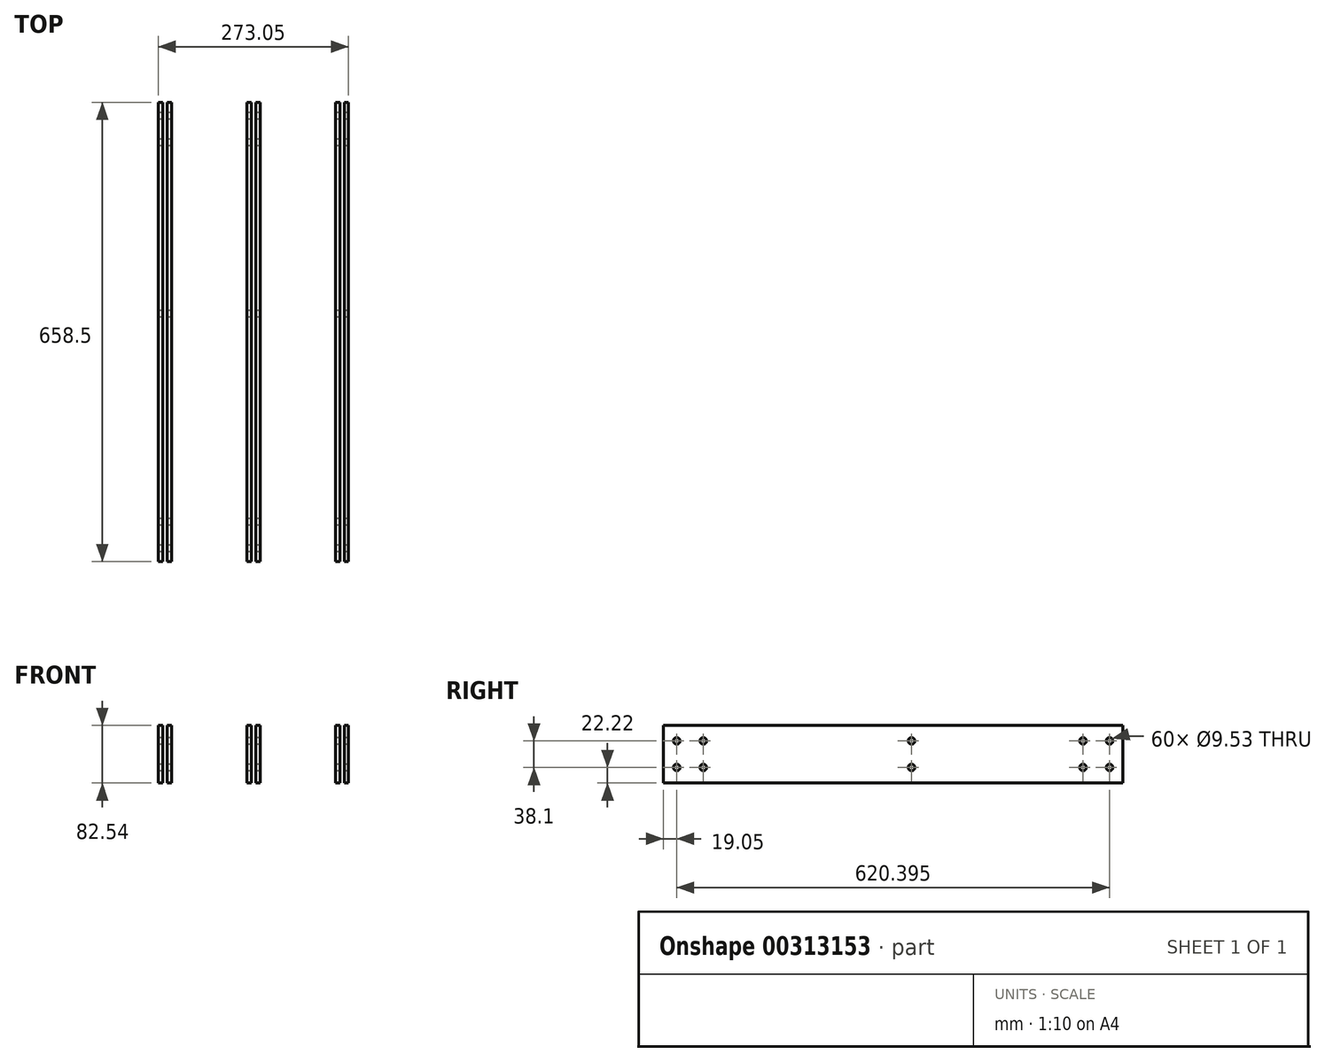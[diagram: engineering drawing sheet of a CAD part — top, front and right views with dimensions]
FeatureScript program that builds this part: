
annotation { "Feature Type Name" : "Feature", "Feature Type Description" : "" }
export const myFeature = defineFeature(function(context is Context, id is Id, definition is map)
    precondition{}
    {
        {
            var Q0;
            Q0=qCreatedBy(makeId("Top.planeOp"),FACE);
            var sketch = newSketch(context, id + "F0", { "sketchPlane" : qUnion([Q0])});
            skLineSegment(sketch, "E0.bottom", {"start": v(0, 0) * mm, "end": v(6.35, 0) * mm});
            skLineSegment(sketch, "E0.top", {"start": v(0, 658.5) * mm, "end": v(6.35, 658.5) * mm});
            skLineSegment(sketch, "E0.left", {"start": v(0, 0) * mm, "end": v(0, 658.5) * mm});
            skLineSegment(sketch, "E0.right", {"start": v(6.35, 0) * mm, "end": v(6.35, 658.5) * mm});
            skLineSegment(sketch, "E1.1.0.0", {"start": v(133.35, 0) * mm, "end": v(133.35, 658.5) * mm});
            skLineSegment(sketch, "E1.1.0.1", {"start": v(127, 0) * mm, "end": v(127, 658.5) * mm});
            skLineSegment(sketch, "E1.1.0.2", {"start": v(127, 658.5) * mm, "end": v(133.35, 658.5) * mm});
            skLineSegment(sketch, "E1.1.0.3", {"start": v(127, 0) * mm, "end": v(133.35, 0) * mm});
            skLineSegment(sketch, "E1.2.0.0", {"start": v(260.35, 0) * mm, "end": v(260.35, 658.5) * mm});
            skLineSegment(sketch, "E1.2.0.1", {"start": v(254, 0) * mm, "end": v(254, 658.5) * mm});
            skLineSegment(sketch, "E1.2.0.2", {"start": v(254, 658.5) * mm, "end": v(260.35, 658.5) * mm});
            skLineSegment(sketch, "E1.2.0.3", {"start": v(254, 0) * mm, "end": v(260.35, 0) * mm});
            skLineSegment(sketch, "E1.direction1", {"start": v(0, 0) * mm, "end": v(127, 0) * mm, "construction": true});
            skSolve(sketch);
        }
        {
            var Q0;
            Q0=qCreatedBy(makeId("Top.planeOp"),FACE);
            var sketch = newSketch(context, id + "F1", { "sketchPlane" : qUnion([Q0])});
            skLineSegment(sketch, "E2.bottom", {"start": v(12.7, 0) * mm, "end": v(19.05, 0) * mm});
            skLineSegment(sketch, "E2.top", {"start": v(12.7, 658.5) * mm, "end": v(19.05, 658.5) * mm});
            skLineSegment(sketch, "E2.left", {"start": v(12.7, 0) * mm, "end": v(12.7, 658.5) * mm});
            skLineSegment(sketch, "E2.right", {"start": v(19.05, 0) * mm, "end": v(19.05, 658.5) * mm});
            skLineSegment(sketch, "E3.1.0.0", {"start": v(146.05, 0) * mm, "end": v(146.05, 658.5) * mm});
            skLineSegment(sketch, "E3.1.0.1", {"start": v(139.7, 0) * mm, "end": v(139.7, 658.5) * mm});
            skLineSegment(sketch, "E3.1.0.2", {"start": v(139.7, 658.5) * mm, "end": v(146.05, 658.5) * mm});
            skLineSegment(sketch, "E3.1.0.3", {"start": v(139.7, 0) * mm, "end": v(146.05, 0) * mm});
            skLineSegment(sketch, "E3.2.0.0", {"start": v(273.05, 0) * mm, "end": v(273.05, 658.5) * mm});
            skLineSegment(sketch, "E3.2.0.1", {"start": v(266.7, 0) * mm, "end": v(266.7, 658.5) * mm});
            skLineSegment(sketch, "E3.2.0.2", {"start": v(266.7, 658.5) * mm, "end": v(273.05, 658.5) * mm});
            skLineSegment(sketch, "E3.2.0.3", {"start": v(266.7, 0) * mm, "end": v(273.05, 0) * mm});
            skLineSegment(sketch, "E3.direction1", {"start": v(12.7, 0) * mm, "end": v(139.7, 0) * mm, "construction": true});
            skSolve(sketch);
        }
        {
            var Q0;
            Q0=qSketchRegion(id+"F0",true);
            var Q1;
            Q1=qSketchRegion(id+"F1",true);
            extrude(context, id + "F2", {"entities" : qUnion([Q0, Q1]), "endBound" : BoundingType.SYMMETRIC, "depth" : 82.55 * mm});
        }
        {
            var Q0;
            Q0=makeQuery(id+"F2.opExtrude","SWEPT_FACE",FACE,{"disambiguationData":[OSD([sQuery(id+"F0.wireOp",EDGE,"E0.left")])]});
            var sketch = newSketch(context, id + "F3", { "sketchPlane" : qUnion([Q0])});
            skCircle(sketch, "E4", {"center": v(-19.05, 19.05) * mm, "radius": 4.76 * mm});
            skCircle(sketch, "E5", {"center": v(-57.15, 19.05) * mm, "radius": 4.76 * mm});
            skCircle(sketch, "E6", {"center": v(-57.15, -19.05) * mm, "radius": 4.76 * mm});
            skCircle(sketch, "E7", {"center": v(-19.05, -19.05) * mm, "radius": 4.76 * mm});
            skCircle(sketch, "E8.1.0.0", {"center": v(-639.45, 19.05) * mm, "radius": 4.76 * mm});
            skCircle(sketch, "E8.1.0.1", {"center": v(-601.35, 19.05) * mm, "radius": 4.76 * mm});
            skCircle(sketch, "E8.1.0.2", {"center": v(-601.35, -19.05) * mm, "radius": 4.76 * mm});
            skCircle(sketch, "E8.1.0.3", {"center": v(-639.45, -19.05) * mm, "radius": 4.76 * mm});
            skCircle(sketch, "E9", {"center": v(-355.6, 19.05) * mm, "radius": 4.76 * mm});
            skCircle(sketch, "E10", {"center": v(-355.6, -19.05) * mm, "radius": 4.76 * mm});
            skSolve(sketch);
        }
        {
            var Q0;
            Q0=qSketchRegion(id+"F3",true);
            extrude(context, id + "F4", {"entities" : qUnion([Q0]), "operationType" : NewBodyOperationType.REMOVE, "endBound" : BoundingType.THROUGH_ALL, "oppositeDirection" : true, "depth" : 25.4 * mm});
        }
    });
